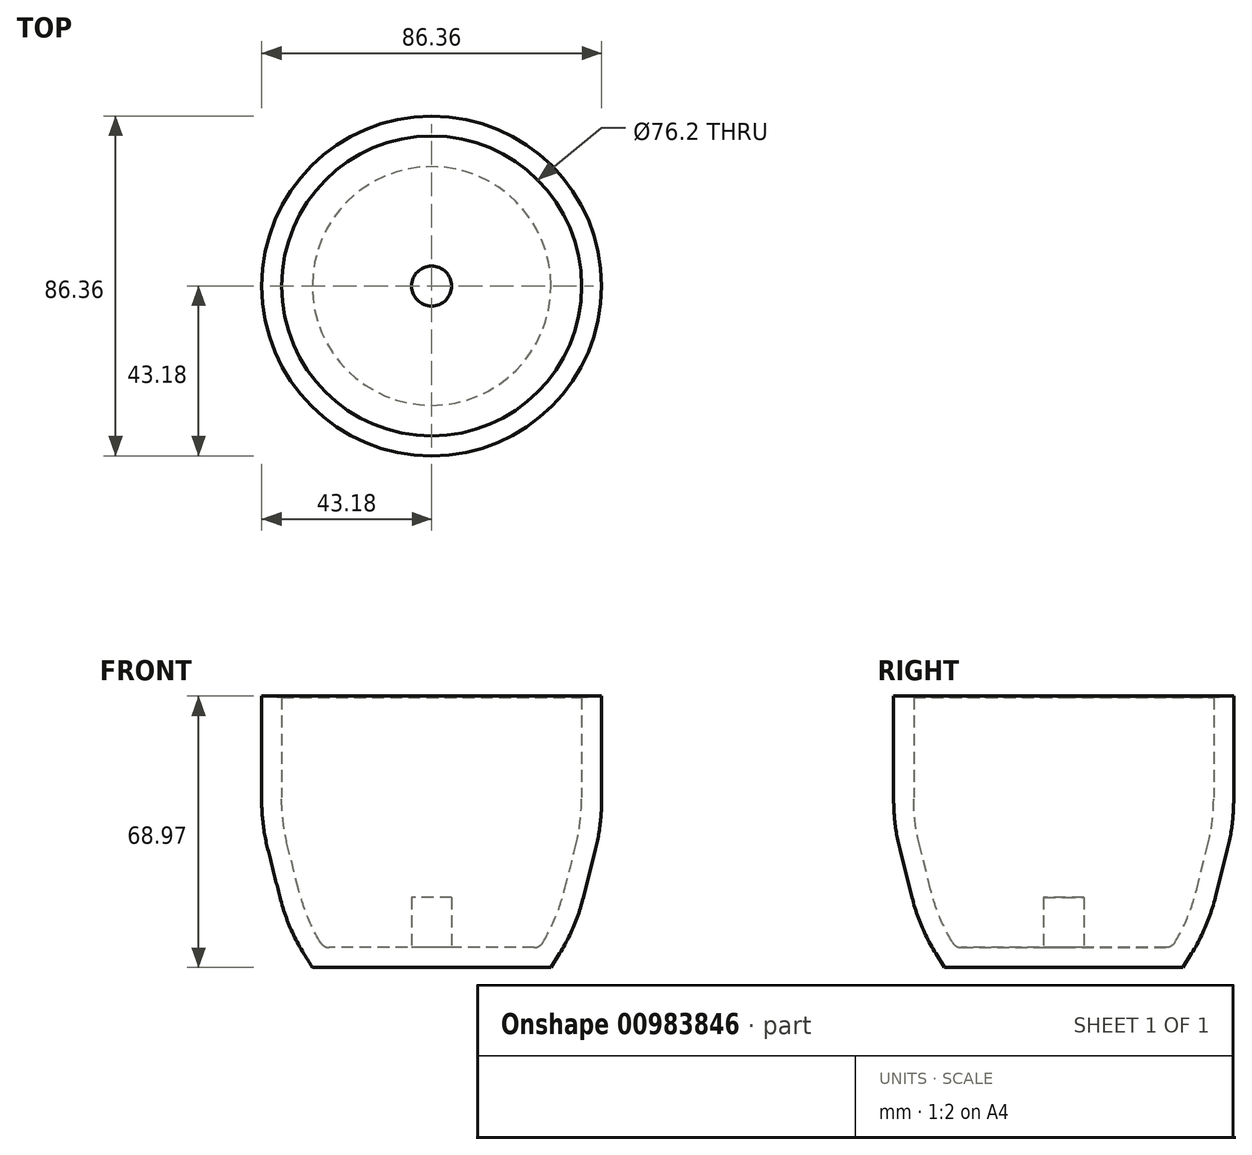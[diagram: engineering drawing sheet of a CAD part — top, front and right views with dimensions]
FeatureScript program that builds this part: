
annotation { "Feature Type Name" : "Feature", "Feature Type Description" : "" }
export const myFeature = defineFeature(function(context is Context, id is Id, definition is map)
    precondition{}
    {
        {
            var Q0;
            Q0=qCreatedBy(makeId("Front.planeOp"),FACE);
            var sketch = newSketch(context, id + "F0", { "sketchPlane" : qUnion([Q0])});
            skLineSegment(sketch, "E0", {"start": v(0, 0) * mm, "end": v(0, 63.5) * mm, "construction": true});
            skLineSegment(sketch, "E1", {"start": v(0, 63.5) * mm, "end": v(38.1, 63.5) * mm, "construction": true});
            skLineSegment(sketch, "E2", {"start": v(38.1, 63.5) * mm, "end": v(38.1, 31.75) * mm});
            skLineSegment(sketch, "E3", {"start": v(38.1, 31.75) * mm, "end": v(31.88, 7.12) * mm});
            skLineSegment(sketch, "E4", {"start": v(31.88, 7.12) * mm, "end": v(27.48, 0) * mm});
            skLineSegment(sketch, "E5", {"start": v(27.48, 0) * mm, "end": v(0, 0) * mm});
            skLineSegment(sketch, "E6.0", {"start": v(30.31, -5.08) * mm, "end": v(0, -5.08) * mm});
            skLineSegment(sketch, "E6.1", {"start": v(36.6, 5.12) * mm, "end": v(30.31, -5.08) * mm});
            skLineSegment(sketch, "E6.2", {"start": v(43.18, 31.12) * mm, "end": v(36.6, 5.12) * mm});
            skLineSegment(sketch, "E6.3", {"start": v(43.18, 63.9) * mm, "end": v(43.18, 31.12) * mm});
            skLineSegment(sketch, "E7", {"start": v(38.1, 63.5) * mm, "end": v(43.18, 63.9) * mm});
            skLineSegment(sketch, "E8", {"start": v(0, 0) * mm, "end": v(0, -5.08) * mm});
            skSolve(sketch);
        }
        {
            var Q0;
            Q0=makeQuery(id+"F0.imprint","IMPRINT",FACE,{"disambiguationData":[TD([[makeQuery(id+"F0.imprint","IMPRINT",EDGE,{"derivedFrom":sQuery(id+"F0.wireOp",EDGE,"E2")}),1.0]])]});
            var Q1;
            Q1=sQuery(id+"F0.wireOp",EDGE,"E0");
            revolve(context, id + "F1", {"surfaceOperationType" : NewSurfaceOperationType.NEW, "entities" : qUnion([Q0]), "axis" : qUnion([Q1]), "revolveType" : RevolveType.FULL});
        }
        {
            var Q0;
            Q0=makeQuery(id+"F1.opRevolve","SWEPT_EDGE",EDGE,{"disambiguationData":[OSD([sQuery(id+"F0.wireOp",EDGE,"E6.2"),sQuery(id+"F0.wireOp",EDGE,"E6.3")])]});
            var Q1;
            Q1=makeQuery(id+"F1.opRevolve","SWEPT_EDGE",EDGE,{"disambiguationData":[OSD([sQuery(id+"F0.wireOp",EDGE,"E6.1"),sQuery(id+"F0.wireOp",EDGE,"E6.2")])]});
            fillet(context, id + "F2", {"entities" : qUnion([Q0, Q1]), "radius" : 50.8 * mm, "tangentPropagation" : true, "allowEdgeOverflow" : false});
        }
        {
            var Q0;
            Q0=makeQuery(id+"F1.opRevolve","SWEPT_EDGE",EDGE,{"disambiguationData":[OSD([sQuery(id+"F0.wireOp",EDGE,"E2"),sQuery(id+"F0.wireOp",EDGE,"E3")])]});
            var Q1;
            Q1=makeQuery(id+"F1.opRevolve","SWEPT_EDGE",EDGE,{"disambiguationData":[OSD([sQuery(id+"F0.wireOp",EDGE,"E3"),sQuery(id+"F0.wireOp",EDGE,"E4")])]});
            fillet(context, id + "F3", {"entities" : qUnion([Q0, Q1]), "radius" : 50.8 * mm, "tangentPropagation" : true, "allowEdgeOverflow" : false});
        }
        {
            var Q0;
            Q0=makeQuery(id+"F1.opRevolve","SWEPT_EDGE",EDGE,{"disambiguationData":[OSD([sQuery(id+"F0.wireOp",EDGE,"E4"),sQuery(id+"F0.wireOp",EDGE,"E5")])]});
            fillet(context, id + "F4", {"entities" : qUnion([Q0]), "radius" : 2.54 * mm, "tangentPropagation" : true, "allowEdgeOverflow" : false});
        }
        {
            var Q0;
            Q0=makeQuery(id+"F1.opRevolve","SWEPT_FACE",FACE,{"disambiguationData":[OSD([sQuery(id+"F0.wireOp",EDGE,"E5")])]});
            var sketch = newSketch(context, id + "F5", { "sketchPlane" : qUnion([Q0])});
            skCircle(sketch, "E9", {"center": v(0, 0) * mm, "radius": 5.08 * mm});
            skSolve(sketch);
        }
        {
            var Q0;
            Q0 = qSketchRegion(id + "F5", true);
            extrude(context, id + "F6", {"entities" : qUnion([Q0]), "operationType" : NewBodyOperationType.ADD, "depth" : 12.7 * mm, "offsetDistance" : 25.4 * mm});
        }
    });
